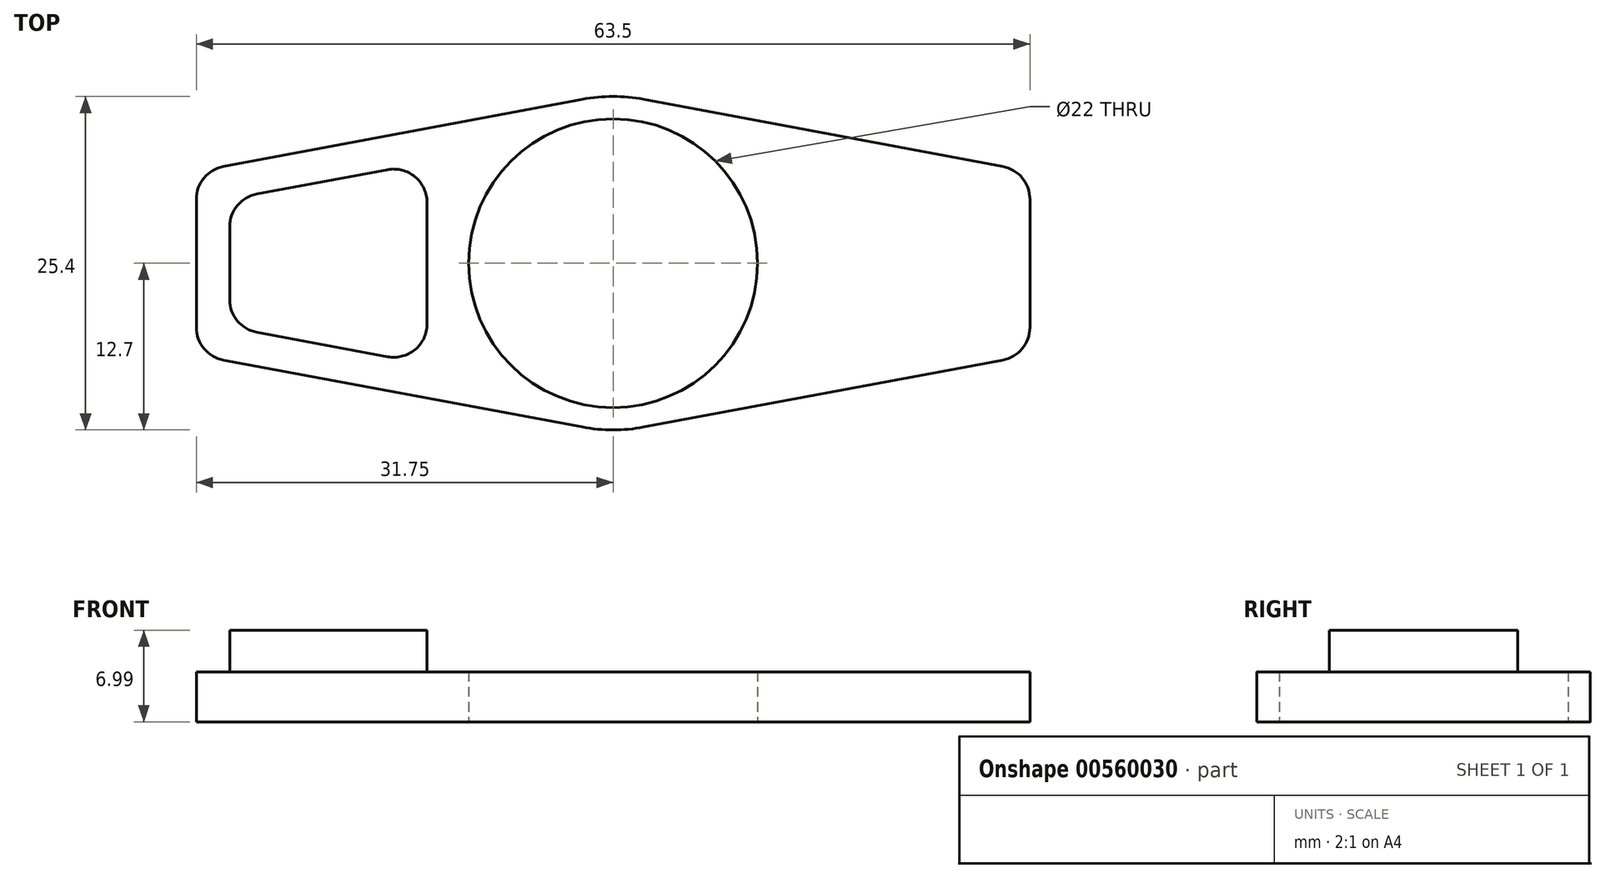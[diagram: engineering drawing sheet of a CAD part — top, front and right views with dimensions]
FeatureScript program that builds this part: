
annotation { "Feature Type Name" : "Feature", "Feature Type Description" : "" }
export const myFeature = defineFeature(function(context is Context, id is Id, definition is map)
    precondition{}
    {
        {
            var Q0;
            Q0=qCreatedBy(makeId("Top.planeOp"),FACE);
            var sketch = newSketch(context, id + "F0", { "sketchPlane" : qUnion([Q0])});
            skCircle(sketch, "E0", {"center": v(0, 0) * mm, "radius": 11 * mm});
            skArc(sketch, "E1", {"start": v(-2.33, -12.48) * mm, "mid": v(0, -12.7) * mm, "end": v(2.33, -12.48) * mm});
            skCircle(sketch, "E2", {"center": v(0, 0) * mm, "radius": 8 * mm, "construction": true});
            skLineSegment(sketch, "E3", {"start": v(2.33, 12.48) * mm, "end": v(31.75, 6.99) * mm});
            skLineSegment(sketch, "E4", {"start": v(31.75, 6.99) * mm, "end": v(31.75, -6.99) * mm});
            skLineSegment(sketch, "E5", {"start": v(31.75, -6.99) * mm, "end": v(2.33, -12.48) * mm});
            skLineSegment(sketch, "E6", {"start": v(0, 0) * mm, "end": v(73.48, 0) * mm, "construction": true});
            skLineSegment(sketch, "E7", {"start": v(0, 0) * mm, "end": v(0, 26.47) * mm, "construction": true});
            skLineSegment(sketch, "E8.MirrorCS", {"start": v(-31.75, -6.99) * mm, "end": v(-2.33, -12.48) * mm});
            skLineSegment(sketch, "E9.MirrorCS", {"start": v(-31.75, 6.99) * mm, "end": v(-31.75, -6.99) * mm});
            skLineSegment(sketch, "E10.MirrorCS", {"start": v(-2.33, 12.48) * mm, "end": v(-31.75, 6.99) * mm});
            skArc(sketch, "E11.trimOffspring", {"start": v(2.33, 12.48) * mm, "mid": v(0, 12.7) * mm, "end": v(-2.33, 12.48) * mm});
            skSolve(sketch);
        }
        {
            var Q0;
            Q0=qSketchRegion(id+"F0",true);
            extrude(context, id + "F1", {"entities" : qUnion([Q0]), "endBound" : BoundingType.SYMMETRIC, "depth" : 3.8 * mm});
        }
        {
            var Q0;
            Q0=makeQuery(id+"F1.opExtrude","CAP_FACE",FACE,{"disambiguationData":[OSD([sQuery(id+"F0.wireOp",EDGE,"E0"),sQuery(id+"F0.wireOp",EDGE,"E1"),sQuery(id+"F0.wireOp",EDGE,"E3"),sQuery(id+"F0.wireOp",EDGE,"E4"),sQuery(id+"F0.wireOp",EDGE,"E5"),sQuery(id+"F0.wireOp",EDGE,"E8.MirrorCS"),sQuery(id+"F0.wireOp",EDGE,"E9.MirrorCS"),sQuery(id+"F0.wireOp",EDGE,"E10.MirrorCS"),sQuery(id+"F0.wireOp",EDGE,"E11.trimOffspring")])],"isStart":false});
            var sketch = newSketch(context, id + "F2", { "sketchPlane" : qUnion([Q0])});
            skLineSegment(sketch, "E12.0", {"start": v(-29.21, -4.88) * mm, "end": v(-14.17, -7.69) * mm});
            skLineSegment(sketch, "E12.1", {"start": v(-29.21, 4.88) * mm, "end": v(-29.21, -4.88) * mm});
            skLineSegment(sketch, "E12.2", {"start": v(-14.18, 7.69) * mm, "end": v(-29.21, 4.88) * mm});
            skLineSegment(sketch, "E13", {"start": v(-14.18, 7.69) * mm, "end": v(-14.17, -7.69) * mm});
            skSolve(sketch);
        }
        {
            var Q0;
            Q0=makeQuery(id+"F1.opExtrude","SWEPT_EDGE",EDGE,{"disambiguationData":[OSD([sQuery(id+"F0.wireOp",EDGE,"E9.MirrorCS"),sQuery(id+"F0.wireOp",EDGE,"E10.MirrorCS")])]});
            var Q1;
            Q1=makeQuery(id+"F1.opExtrude","SWEPT_EDGE",EDGE,{"disambiguationData":[OSD([sQuery(id+"F0.wireOp",EDGE,"E8.MirrorCS"),sQuery(id+"F0.wireOp",EDGE,"E9.MirrorCS")])]});
            var Q2;
            Q2=makeQuery(id+"F1.opExtrude","SWEPT_EDGE",EDGE,{"disambiguationData":[OSD([sQuery(id+"F0.wireOp",EDGE,"E4"),sQuery(id+"F0.wireOp",EDGE,"E5")])]});
            var Q3;
            Q3=makeQuery(id+"F1.opExtrude","SWEPT_EDGE",EDGE,{"disambiguationData":[OSD([sQuery(id+"F0.wireOp",EDGE,"E3"),sQuery(id+"F0.wireOp",EDGE,"E4")])]});
            fillet(context, id + "F3", {"entities" : qUnion([Q0, Q1, Q2, Q3]), "radius" : 2.54 * mm, "tangentPropagation" : true, "allowEdgeOverflow" : false});
        }
        {
            var Q0;
            Q0=qSketchRegion(id+"F2",true);
            extrude(context, id + "F4", {"entities" : qUnion([Q0]), "operationType" : NewBodyOperationType.ADD, "depth" : 3.17 * mm});
        }
        {
            var Q0;
            Q0=makeQuery(id+"F4.opExtrude","SWEPT_EDGE",EDGE,{"disambiguationData":[OSD([sQuery(id+"F2.wireOp",EDGE,"E12.0"),sQuery(id+"F2.wireOp",EDGE,"E12.1")])]});
            var Q1;
            Q1=makeQuery(id+"F4.opExtrude","SWEPT_EDGE",EDGE,{"disambiguationData":[OSD([sQuery(id+"F2.wireOp",EDGE,"E12.0"),sQuery(id+"F2.wireOp",EDGE,"E13")])]});
            var Q2;
            Q2=makeQuery(id+"F4.opExtrude","SWEPT_EDGE",EDGE,{"disambiguationData":[OSD([sQuery(id+"F2.wireOp",EDGE,"E12.2"),sQuery(id+"F2.wireOp",EDGE,"E13")])]});
            var Q3;
            Q3=makeQuery(id+"F4.opExtrude","SWEPT_EDGE",EDGE,{"disambiguationData":[OSD([sQuery(id+"F2.wireOp",EDGE,"E12.1"),sQuery(id+"F2.wireOp",EDGE,"E12.2")])]});
            fillet(context, id + "F5", {"entities" : qUnion([Q0, Q1, Q2, Q3]), "radius" : 2.54 * mm, "tangentPropagation" : true, "allowEdgeOverflow" : false});
        }
    });
